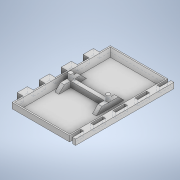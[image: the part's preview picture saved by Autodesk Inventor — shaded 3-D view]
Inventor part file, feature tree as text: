
AUTODESK INVENTOR PART (.ipt)
format: ipt  version: 2020.1 (Build 241239000, 239)  size: 362,496 bytes
history: native  units: mm
features: extrude x7, sketch x7, projected_geometry x4, chamfer x2
ambient origin geometry x8: Origin, YZ Plane, XZ Plane, XY Plane, X Axis, Y Axis, Z Axis, Center Point
bodies: Solid1 (feature_tree)
feature tree (20):
  extrude  "Extrusion1"  Depth=90.0mm
  extrude  "Extrusion2"  Depth=5.419mm
  extrude  "Extrusion3"  Depth=5.419mm
  extrude  "Extrusion4"  Depth=50.0mm
  chamfer  "Chamfer1"  Distance=5.0mm
  extrude  "Tolerances Extrusion "  Depth=3.419mm
  extrude  "Extrusion10"  Depth=2.0mm
  extrude  "Extrusion11"  Depth=5.0mm
  chamfer  "Chamfer3"  Distance=4.0mm
  sketch  "Sketch1"  dims[d0=63.837mm d1=90.0mm]
  sketch  "Sketch2"  dims[d2=5.0mm d3=0.0mm d4=5.419mm]
  sketch  "Sketch3"  dims[d5=10.0mm d6=5.419mm]
  sketch  "Sketch4"  dims[d7=10.0mm d8=50.0mm d10=20.0mm d11=10.0mm d13=10.0mm d15=5.0mm d16=0.0mm]
  projected_geometry  "Projected Loop1"
  sketch  "Sketch9"  dims[d17=90.0mm d18=3.419mm]
  projected_geometry  "Projected Loop10"
  projected_geometry  "Projected Loop11"
  sketch  "Sketch11"  dims[d19=0.0mm d20=2.0mm]
  sketch  "Sketch12"  dims[d21=5.0mm d22=0.0mm d23=5.5mm d24=4.0mm d25=0.0mm d26=4.0mm d27=2.0mm d28=45.0deg d55=0.3mm d56=0.3mm d57=0.3mm d58=0.3mm d59=5.0mm d60=0.0mm d76=3.65mm d77=3.65mm d78=17.05mm d79=17.05mm d80=44.2mm d81=44.2mm d82=10.0mm d83=0.0mm d84=25.0mm d85=25.0mm d86=5.0mm d87=0.0mm d88=5.0mm d89=5.0mm d90=45.0deg d61=0.5mm d62=0.872665mm d63=0.5mm d64=0.872665mm]
  projected_geometry  "Projected Loop12"
